# Revit family: ВУТР ВЕ_Eng
name_source: partatom
category: Mechanical Equipment
units: mm (PartAtom-declared; Revit-internal decimal feet)

## family parameters
Always vertical = Yes
Classification = None
Cut with Voids When Loaded = No
Part Type = Normal
Room Calculation Point = No
Round Connector Dimension = Use Diameter
Shared = No
Work Plane-Based = No

## types (8) — shared parameters
00_20_Manufacturer = Vents
00_20_Name = Air handling units with heat recovery
A = 50 mm  [stored 0.164042 ft]
Casing Material = Metal, painted, white, matte
Filter = G4, F7
Frequency = 50 Hz
Load Classification = HVAC
Maintenance zone material = <By Category>
Manufacturer = Vents
Number of Fase = 1
URL = https://ventilation-system.com
Voltage = 230 V
zero-valued in all types: Default Elevation

## per-type parameters (varying)
- VUTR 400 VЕ EC А21: Amperage=8 A; Apparent Load=1725 VA; B=528 mm; B1=149 mm  [stored 0.488845 ft]; B11=149 mm  [stored 0.488845 ft]; B12=149 mm  [stored 0.488845 ft]; B13=149 mm  [stored 0.488845 ft]; B21=111 mm; D1=100 mm  [stored 0.328084 ft]; D1n=105 mm  [stored 0.344488 ft]; Diameter=160 mm  [stored 0.524934 ft]; Dn=165 mm; Dy=160 mm  [stored 0.524934 ft]; EB=260 mm  [stored 0.853018 ft]; EL=420 mm; H=755 mm; H1=695 mm; Height=755 mm; L=745 mm; L1=167 mm  [stored 0.5479 ft]; L11=167 mm  [stored 0.5479 ft]; L12=167 mm  [stored 0.5479 ft]; L13=167 mm  [stored 0.5479 ft]; L21=373 mm; Leg=Yes; Length=745 mm; Maximum Air Flow=440.0 m³/h; Power=1600 W; SB1=290 mm  [stored 0.951444 ft]; SB2=240 mm  [stored 0.787402 ft]; SB3=190 mm  [stored 0.62336 ft]; SL1=480 mm; SL2=480 mm; SL3=480 mm; Sound pressure level at 3 m distance=33 dBA; Weight=82.00 kg; Width=528 mm; h=20 mm  [stored 0.0656168 ft]
- VUTR 400 V EC А21: Amperage=1 A; Apparent Load=322 VA; B=528 mm; B1=149 mm  [stored 0.488845 ft]; B11=149 mm  [stored 0.488845 ft]; B12=149 mm  [stored 0.488845 ft]; B13=149 mm  [stored 0.488845 ft]; B21=111 mm; D1=100 mm  [stored 0.328084 ft]; D1n=105 mm  [stored 0.344488 ft]; Diameter=160 mm  [stored 0.524934 ft]; Dn=165 mm; Dy=160 mm  [stored 0.524934 ft]; EB=260 mm  [stored 0.853018 ft]; EL=420 mm; H=755 mm; H1=695 mm; Height=755 mm; L=745 mm; L1=167 mm  [stored 0.5479 ft]; L11=167 mm  [stored 0.5479 ft]; L12=167 mm  [stored 0.5479 ft]; L13=167 mm  [stored 0.5479 ft]; L21=373 mm; Leg=Yes; Length=745 mm; Maximum Air Flow=440.0 m³/h; Power=200 W; SB1=290 mm  [stored 0.951444 ft]; SB2=240 mm  [stored 0.787402 ft]; SB3=190 mm  [stored 0.62336 ft]; SL1=480 mm; SL2=480 mm; SL3=480 mm; Sound pressure level at 3 m distance=33 dBA; Weight=81.00 kg; Width=528 mm; h=20 mm  [stored 0.0656168 ft]
- VUTR 600 V EC А21: Amperage=3 A; Apparent Load=598 VA; B=628 mm; B1=183 mm; B11=183 mm; B12=183 mm; B13=183 mm; B21=126 mm  [stored 0.413386 ft]; D1=125 mm  [stored 0.410105 ft]; D1n=130 mm  [stored 0.426509 ft]; Diameter=200 mm  [stored 0.656168 ft]; Dn=205 mm  [stored 0.672572 ft]; Dy=200 mm  [stored 0.656168 ft]; EB=330 mm; EL=450 mm; H=852 mm; H1=792 mm; Height=852 mm; L=819 mm; L1=167 mm  [stored 0.5479 ft]; L11=167 mm  [stored 0.5479 ft]; L12=167 mm  [stored 0.5479 ft]; L13=167 mm  [stored 0.5479 ft]; L21=410 mm; Leg=Yes; Length=819 mm; Maximum Air Flow=670.0 m³/h; Power=405 W; SB1=314 mm  [stored 1.03018 ft]; SB2=264 mm  [stored 0.866142 ft]; SB3=364 mm; SL1=520 mm; SL2=520 mm; SL3=520 mm; Sound pressure level at 3 m distance=35 dBA; Weight=90.00 kg; Width=628 mm; h=20 mm  [stored 0.0656168 ft]
- VUTR 600 VЕ EC А21: Amperage=15 A; Apparent Load=3404 VA; B=628 mm; B1=183 mm; B11=183 mm; B12=183 mm; B13=183 mm; B21=126 mm  [stored 0.413386 ft]; D1=125 mm  [stored 0.410105 ft]; D1n=130 mm  [stored 0.426509 ft]; Diameter=200 mm  [stored 0.656168 ft]; Dn=205 mm  [stored 0.672572 ft]; Dy=200 mm  [stored 0.656168 ft]; EB=330 mm; EL=450 mm; H=852 mm; H1=792 mm; Height=852 mm; L=819 mm; L1=167 mm  [stored 0.5479 ft]; L11=167 mm  [stored 0.5479 ft]; L12=167 mm  [stored 0.5479 ft]; L13=167 mm  [stored 0.5479 ft]; L21=410 mm; Leg=Yes; Length=819 mm; Maximum Air Flow=670.0 m³/h; Power=3205 W; SB1=314 mm  [stored 1.03018 ft]; SB2=264 mm  [stored 0.866142 ft]; SB3=364 mm; SL1=520 mm; SL2=520 mm; SL3=520 mm; Sound pressure level at 3 m distance=35 dBA; Weight=92.00 kg; Width=628 mm; h=20 mm  [stored 0.0656168 ft]
- VUTR 280 V EC А21: Amperage=2 A; Apparent Load=437 VA; B=520 mm; B1=365 mm; B11=385 mm; B12=116 mm  [stored 0.380577 ft]; B13=155 mm  [stored 0.50853 ft]; B21=365 mm; D1=100 mm  [stored 0.328084 ft]; D1n=105 mm  [stored 0.344488 ft]; Diameter=125 mm  [stored 0.410105 ft]; Dn=130 mm  [stored 0.426509 ft]; Dy=125 mm  [stored 0.410105 ft]; EB=230 mm  [stored 0.754593 ft]; EL=330 mm; H=754 mm; H1=650 mm; Height=754 mm; L=598 mm; L1=350 mm  [stored 1.14829 ft]; L11=235 mm  [stored 0.770997 ft]; L12=107 mm  [stored 0.35105 ft]; L13=491 mm; L21=491 mm; Leg=Yes; Length=598 mm; Maximum Air Flow=300.0 m³/h; Power=195 W; SB1=260 mm  [stored 0.853018 ft]; SB2=210 mm  [stored 0.688976 ft]; SB3=160 mm  [stored 0.524934 ft]; SL1=380 mm; SL2=380 mm; SL3=380 mm; Sound pressure level at 3 m distance=26 dBA; Weight=63.00 kg; Width=520 mm; h=20 mm  [stored 0.0656168 ft]
- VUTR 280 VЕ EC А21: Amperage=5 A; Apparent Load=1081 VA; B=520 mm; B1=365 mm; B11=385 mm; B12=116 mm  [stored 0.380577 ft]; B13=155 mm  [stored 0.50853 ft]; B21=365 mm; D1=100 mm  [stored 0.328084 ft]; D1n=105 mm  [stored 0.344488 ft]; Diameter=125 mm  [stored 0.410105 ft]; Dn=130 mm  [stored 0.426509 ft]; Dy=125 mm  [stored 0.410105 ft]; EB=230 mm  [stored 0.754593 ft]; EL=330 mm; H=754 mm; H1=650 mm; Height=754 mm; L=598 mm; L1=350 mm  [stored 1.14829 ft]; L11=235 mm  [stored 0.770997 ft]; L12=107 mm  [stored 0.35105 ft]; L13=491 mm; L21=491 mm; Leg=Yes; Length=598 mm; Maximum Air Flow=300.0 m³/h; Power=845 W; SB1=260 mm  [stored 0.853018 ft]; SB2=210 mm  [stored 0.688976 ft]; SB3=160 mm  [stored 0.524934 ft]; SL1=380 mm; SL2=380 mm; SL3=380 mm; Sound pressure level at 3 m distance=26 dBA; Weight=63.00 kg; Width=520 mm; h=20 mm  [stored 0.0656168 ft]
- VUTR 200 V2 EC А21: Amperage=1 A; Apparent Load=230 VA; B=347 mm  [stored 1.13845 ft]; B1=234 mm  [stored 0.767717 ft]; B11=113 mm  [stored 0.370735 ft]; B12=95 mm; B13=252 mm  [stored 0.826772 ft]; B21=234 mm  [stored 0.767717 ft]; D1=100 mm  [stored 0.328084 ft]; D1n=105 mm  [stored 0.344488 ft]; Diameter=125 mm  [stored 0.410105 ft]; Dn=130 mm  [stored 0.426509 ft]; Dy=125 mm  [stored 0.410105 ft]; EB=120 mm  [stored 0.393701 ft]; EL=100 mm  [stored 0.328084 ft]; H=750 mm; H1=700 mm; Height=750 mm; L=600 mm; L1=361 mm  [stored 1.18438 ft]; L11=96 mm  [stored 0.314961 ft]; L12=95 mm; L13=363 mm; L21=505 mm; Leg=No; Length=600 mm; Maximum Air Flow=270.0 m³/h; Power=118 W; SB1=55 mm  [stored 0.180446 ft]; SB2=55 mm  [stored 0.180446 ft]; SB3=55 mm  [stored 0.180446 ft]; SL1=50 mm  [stored 0.164042 ft]; SL2=100 mm  [stored 0.328084 ft]; SL3=150 mm; Sound pressure level at 3 m distance=28 dBA; Weight=47.00 kg; Width=347 mm  [stored 1.13845 ft]; h=0 mm  [stored 0 ft]
- VUTR 200 V2Е EC А21: Amperage=4 A; Apparent Load=920 VA; B=347 mm  [stored 1.13845 ft]; B1=234 mm  [stored 0.767717 ft]; B11=113 mm  [stored 0.370735 ft]; B12=95 mm; B13=252 mm  [stored 0.826772 ft]; B21=234 mm  [stored 0.767717 ft]; D1=100 mm  [stored 0.328084 ft]; D1n=105 mm  [stored 0.344488 ft]; Diameter=125 mm  [stored 0.410105 ft]; Dn=130 mm  [stored 0.426509 ft]; Dy=125 mm  [stored 0.410105 ft]; EB=120 mm  [stored 0.393701 ft]; EL=100 mm  [stored 0.328084 ft]; H=750 mm; H1=700 mm; Height=750 mm; L=600 mm; L1=361 mm  [stored 1.18438 ft]; L11=96 mm  [stored 0.314961 ft]; L12=95 mm; L13=363 mm; L21=505 mm; Leg=No; Length=600 mm; Maximum Air Flow=270.0 m³/h; Power=818 W; SB1=55 mm  [stored 0.180446 ft]; SB2=55 mm  [stored 0.180446 ft]; SB3=55 mm  [stored 0.180446 ft]; SL1=50 mm  [stored 0.164042 ft]; SL2=100 mm  [stored 0.328084 ft]; SL3=150 mm; Sound pressure level at 3 m distance=28 dBA; Weight=48.00 kg; Width=347 mm  [stored 1.13845 ft]; h=0 mm  [stored 0 ft]

note: column(s) folded — value = type name in every type: 00_20_Type

note: [stored X ft] marks values corroborated as IEEE doubles in the binary element streams (Revit-internal decimal feet)
